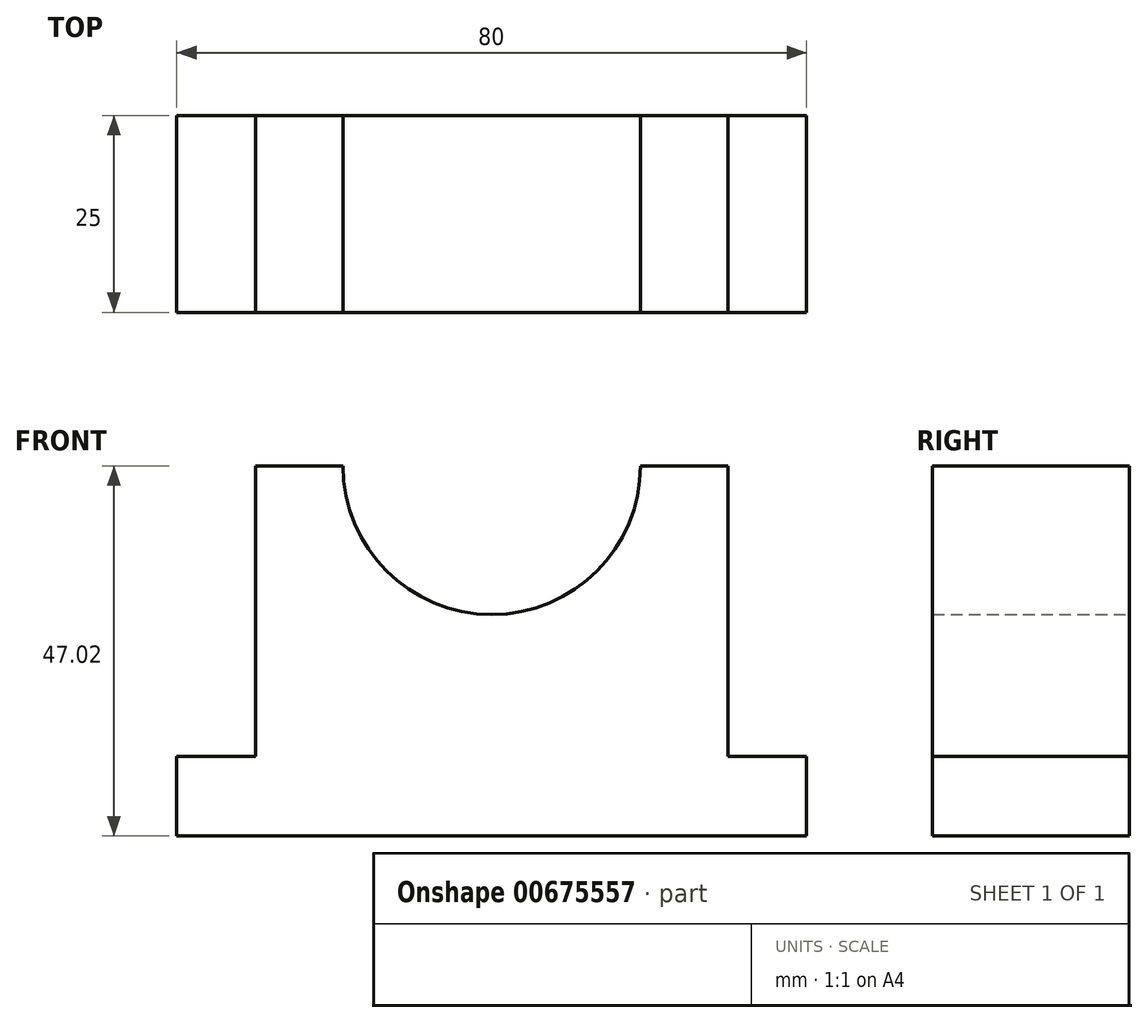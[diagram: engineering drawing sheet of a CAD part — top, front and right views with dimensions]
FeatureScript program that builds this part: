
annotation { "Feature Type Name" : "Feature", "Feature Type Description" : "" }
export const myFeature = defineFeature(function(context is Context, id is Id, definition is map)
    precondition{}
    {
        {
            var Q0;
            Q0=qCreatedBy(makeId("Front.planeOp"),FACE);
            var sketch = newSketch(context, id + "F0", { "sketchPlane" : qUnion([Q0])});
            skLineSegment(sketch, "E0", {"start": v(0, 0) * mm, "end": v(40, 0) * mm});
            skLineSegment(sketch, "E1", {"start": v(40, 0) * mm, "end": v(40, 10.12) * mm});
            skLineSegment(sketch, "E2", {"start": v(40, 10.12) * mm, "end": v(30, 10.12) * mm});
            skLineSegment(sketch, "E3", {"start": v(30, 10.12) * mm, "end": v(30, 47.02) * mm});
            skLineSegment(sketch, "E4", {"start": v(30, 47.02) * mm, "end": v(18.9, 47.02) * mm});
            skLineSegment(sketch, "E5", {"start": v(0, 0) * mm, "end": v(-40, 0) * mm});
            skLineSegment(sketch, "E6", {"start": v(-40, 0) * mm, "end": v(-40, 10.12) * mm});
            skLineSegment(sketch, "E7", {"start": v(-40, 10.12) * mm, "end": v(-30, 10.12) * mm});
            skLineSegment(sketch, "E8", {"start": v(-30, 10.12) * mm, "end": v(-30, 47.02) * mm});
            skLineSegment(sketch, "E9", {"start": v(-30, 47.02) * mm, "end": v(-18.9, 47.02) * mm});
            skArc(sketch, "E10", {"start": v(-18.9, 47.02) * mm, "mid": v(0, 28.12) * mm, "end": v(18.9, 47.02) * mm});
            skSolve(sketch);
        }
        {
            var Q0;
            Q0 = qSketchRegion(id + "F0", true);
            extrude(context, id + "F1", {"entities" : qUnion([Q0]), "depth" : 25 * mm, "offsetDistance" : 25 * mm});
        }
    });
